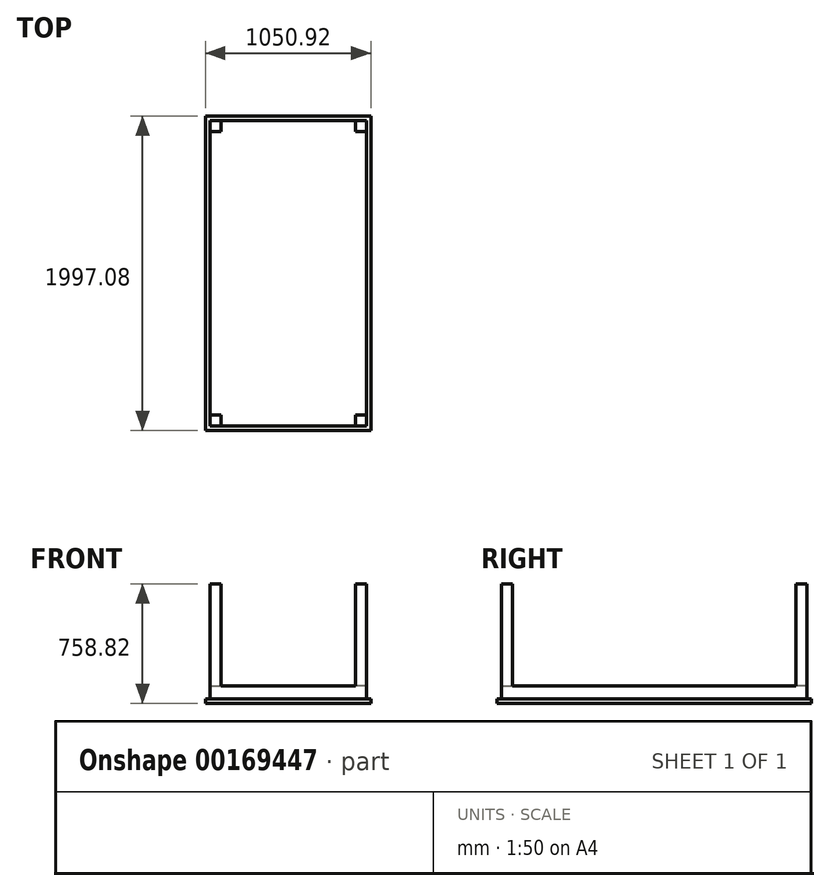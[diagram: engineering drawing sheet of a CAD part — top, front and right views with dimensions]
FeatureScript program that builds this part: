
annotation { "Feature Type Name" : "Feature", "Feature Type Description" : "" }
export const myFeature = defineFeature(function(context is Context, id is Id, definition is map)
    precondition{}
    {
        {
            var Q0;
            Q0=qCreatedBy(makeId("Top.planeOp"),FACE);
            var sketch = newSketch(context, id + "F0", { "sketchPlane" : qUnion([Q0])});
            skLineSegment(sketch, "E0.bottom", {"start": v(-524.15, 1624.42) * mm, "end": v(526.77, 1624.42) * mm});
            skLineSegment(sketch, "E0.top", {"start": v(-524.15, -372.66) * mm, "end": v(526.77, -372.66) * mm});
            skLineSegment(sketch, "E0.left", {"start": v(-524.15, 1624.42) * mm, "end": v(-524.15, -372.66) * mm});
            skLineSegment(sketch, "E0.right", {"start": v(526.77, 1624.42) * mm, "end": v(526.77, -372.66) * mm});
            skSolve(sketch);
        }
        {
            var Q0;
            Q0 = qSketchRegion(id + "F0", true);
            extrude(context, id + "F1", {"entities" : qUnion([Q0]), "depth" : 28.57 * mm});
        }
        {
            var Q0;
            Q0=makeQuery(id+"F1.opExtrude","CAP_FACE",FACE,{"disambiguationData":[OSD([sQuery(id+"F0.wireOp",EDGE,"E0.bottom"),sQuery(id+"F0.wireOp",EDGE,"E0.top"),sQuery(id+"F0.wireOp",EDGE,"E0.left"),sQuery(id+"F0.wireOp",EDGE,"E0.right")])],"isStart":false});
            var sketch = newSketch(context, id + "F2", { "sketchPlane" : qUnion([Q0])});
            skLineSegment(sketch, "E1.bottom", {"start": v(-495.58, 1595.84) * mm, "end": v(498.2, 1595.84) * mm});
            skLineSegment(sketch, "E1.top", {"start": v(-495.58, -344.08) * mm, "end": v(498.2, -344.08) * mm});
            skLineSegment(sketch, "E1.left", {"start": v(-495.58, 1595.84) * mm, "end": v(-495.58, -344.08) * mm});
            skLineSegment(sketch, "E1.right", {"start": v(498.2, 1595.84) * mm, "end": v(498.2, -344.08) * mm});
            skSolve(sketch);
        }
        {
            var Q0;
            Q0 = qSketchRegion(id + "F2", true);
            extrude(context, id + "F3", {"entities" : qUnion([Q0]), "operationType" : NewBodyOperationType.ADD, "depth" : 82.55 * mm});
        }
        {
            var Q0;
            Q0=makeQuery(id+"F3.opExtrude","CAP_FACE",FACE,{"disambiguationData":[OSD([sQuery(id+"F2.wireOp",EDGE,"E1.bottom"),sQuery(id+"F2.wireOp",EDGE,"E1.top"),sQuery(id+"F2.wireOp",EDGE,"E1.left"),sQuery(id+"F2.wireOp",EDGE,"E1.right")])],"isStart":false});
            var sketch = newSketch(context, id + "F4", { "sketchPlane" : qUnion([Q0])});
            skLineSegment(sketch, "E2.bottom", {"start": v(-495.58, 1595.84) * mm, "end": v(-425.73, 1595.84) * mm});
            skLineSegment(sketch, "E2.top", {"start": v(-495.58, 1526) * mm, "end": v(-425.73, 1526) * mm});
            skLineSegment(sketch, "E2.left", {"start": v(-495.58, 1595.84) * mm, "end": v(-495.58, 1526) * mm});
            skLineSegment(sketch, "E2.right", {"start": v(-425.73, 1595.84) * mm, "end": v(-425.73, 1526) * mm});
            skLineSegment(sketch, "E3.bottom", {"start": v(498.2, 1595.84) * mm, "end": v(428.35, 1595.84) * mm});
            skLineSegment(sketch, "E3.top", {"start": v(498.2, 1526) * mm, "end": v(428.35, 1526) * mm});
            skLineSegment(sketch, "E3.left", {"start": v(498.2, 1595.84) * mm, "end": v(498.2, 1526) * mm});
            skLineSegment(sketch, "E3.right", {"start": v(428.35, 1595.84) * mm, "end": v(428.35, 1526) * mm});
            skLineSegment(sketch, "E4.bottom", {"start": v(498.2, -344.08) * mm, "end": v(428.35, -344.08) * mm});
            skLineSegment(sketch, "E4.top", {"start": v(498.2, -274.23) * mm, "end": v(428.35, -274.23) * mm});
            skLineSegment(sketch, "E4.left", {"start": v(498.2, -344.08) * mm, "end": v(498.2, -274.23) * mm});
            skLineSegment(sketch, "E4.right", {"start": v(428.35, -344.08) * mm, "end": v(428.35, -274.23) * mm});
            skLineSegment(sketch, "E5.bottom", {"start": v(-495.58, -344.08) * mm, "end": v(-425.73, -344.08) * mm});
            skLineSegment(sketch, "E5.top", {"start": v(-495.58, -274.23) * mm, "end": v(-425.73, -274.23) * mm});
            skLineSegment(sketch, "E5.left", {"start": v(-495.58, -344.08) * mm, "end": v(-495.58, -274.23) * mm});
            skLineSegment(sketch, "E5.right", {"start": v(-425.73, -344.08) * mm, "end": v(-425.73, -274.23) * mm});
            skSolve(sketch);
        }
        {
            var Q0;
            Q0 = qSketchRegion(id + "F4", true);
            extrude(context, id + "F5", {"entities" : qUnion([Q0]), "operationType" : NewBodyOperationType.ADD, "depth" : 647.7 * mm});
        }
    });
